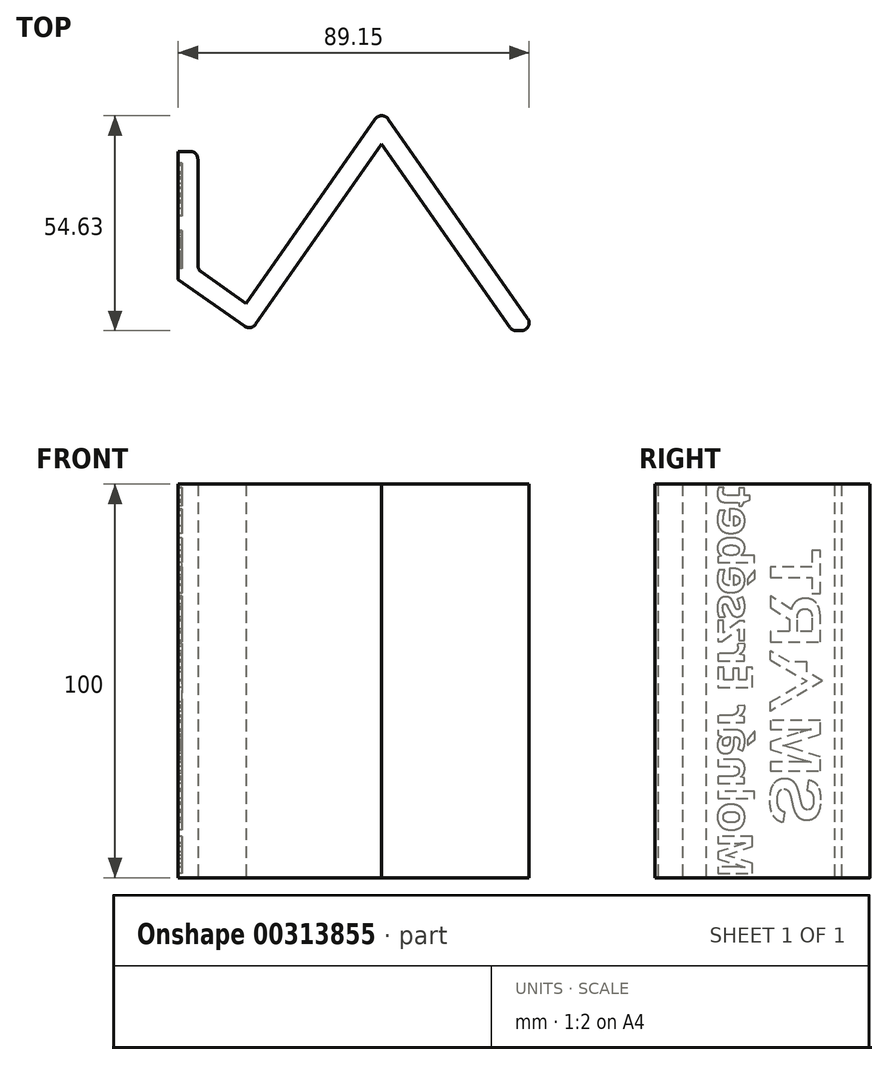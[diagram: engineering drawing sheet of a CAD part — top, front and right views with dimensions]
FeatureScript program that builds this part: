
annotation { "Feature Type Name" : "Feature", "Feature Type Description" : "" }
export const myFeature = defineFeature(function(context is Context, id is Id, definition is map)
    precondition{}
    {
        {
            var Q0;
            Q0=qCreatedBy(makeId("Top.planeOp"),FACE);
            var sketch = newSketch(context, id + "F0", { "sketchPlane" : qUnion([Q0])});
            skLineSegment(sketch, "E0", {"start": v(-30.75, -21.67) * mm, "end": v(-18.46, -30.27) * mm});
            skLineSegment(sketch, "E1", {"start": v(-18.46, -30.27) * mm, "end": v(15.96, 18.88) * mm});
            skLineSegment(sketch, "E2", {"start": v(15.96, 18.88) * mm, "end": v(37.02, -11.21) * mm});
            skLineSegment(sketch, "E3", {"start": v(-30.75, -21.67) * mm, "end": v(-30.75, 8.33) * mm});
            skLineSegment(sketch, "E4", {"start": v(-45.81, -37.24) * mm, "end": v(46.59, -37.24) * mm, "construction": true});
            skLineSegment(sketch, "E5.0", {"start": v(-35.75, -24.27) * mm, "end": v(-35.75, 8.33) * mm});
            skLineSegment(sketch, "E5.1", {"start": v(-35.75, -24.27) * mm, "end": v(-17.23, -37.24) * mm});
            skLineSegment(sketch, "E5.2", {"start": v(-17.23, -37.24) * mm, "end": v(15.96, 10.16) * mm});
            skLineSegment(sketch, "E5.3", {"start": v(15.96, 10.16) * mm, "end": v(49.14, -37.24) * mm});
            skLineSegment(sketch, "E6", {"start": v(-35.75, 8.33) * mm, "end": v(-30.75, 8.33) * mm});
            skLineSegment(sketch, "E7", {"start": v(49.14, -37.24) * mm, "end": v(55.25, -37.24) * mm});
            skLineSegment(sketch, "E8", {"start": v(37.02, -11.21) * mm, "end": v(55.25, -37.24) * mm});
            skSolve(sketch);
        }
        {
            var Q0;
            Q0=makeQuery(id+"F0.imprint","IMPRINT",FACE,{"disambiguationData":[TD([[makeQuery(id+"F0.imprint","IMPRINT",EDGE,{"derivedFrom":sQuery(id+"F0.wireOp",EDGE,"E0")}),-1.0]])]});
            extrude(context, id + "F1", {"entities" : qUnion([Q0]), "depth" : 100 * mm});
        }
        {
            var Q0;
            Q0=makeQuery(id+"F1.opExtrude","SWEPT_EDGE",EDGE,{"disambiguationData":[OSD([sQuery(id+"F0.wireOp",EDGE,"E5.1"),sQuery(id+"F0.wireOp",EDGE,"E5.2")])]});
            var Q1;
            Q1=makeQuery(id+"F1.opExtrude","SWEPT_EDGE",EDGE,{"disambiguationData":[OSD([sQuery(id+"F0.wireOp",EDGE,"E5.3"),sQuery(id+"F0.wireOp",EDGE,"E7")])]});
            var Q2;
            Q2=makeQuery(id+"F1.opExtrude","SWEPT_EDGE",EDGE,{"disambiguationData":[OSD([sQuery(id+"F0.wireOp",EDGE,"E7"),sQuery(id+"F0.wireOp",EDGE,"E8")])]});
            var Q3;
            Q3=makeQuery(id+"F1.opExtrude","SWEPT_EDGE",EDGE,{"disambiguationData":[OSD([sQuery(id+"F0.wireOp",EDGE,"E1"),sQuery(id+"F0.wireOp",EDGE,"E2")])]});
            var Q4;
            Q4=makeQuery(id+"F1.opExtrude","SWEPT_EDGE",EDGE,{"disambiguationData":[OSD([sQuery(id+"F0.wireOp",EDGE,"E0"),sQuery(id+"F0.wireOp",EDGE,"E3")])]});
            var Q5;
            Q5=makeQuery(id+"F1.opExtrude","SWEPT_EDGE",EDGE,{"disambiguationData":[OSD([sQuery(id+"F0.wireOp",EDGE,"E3"),sQuery(id+"F0.wireOp",EDGE,"E6")])]});
            fillet(context, id + "F2", {"entities" : qUnion([Q0, Q1, Q2, Q3, Q4, Q5]), "radius" : 2 * mm, "tangentPropagation" : true, "allowEdgeOverflow" : false});
        }
        {
            var Q0;
            Q0=makeQuery(id+"F1.opExtrude","SWEPT_FACE",FACE,{"disambiguationData":[OSD([sQuery(id+"F0.wireOp",EDGE,"E5.0")])]});
            var sketch = newSketch(context, id + "F3", { "sketchPlane" : qUnion([Q0])});
            skLineSegment(sketch, "E9", {"start": v(24.27, 50) * mm, "end": v(-8.33, 50) * mm, "construction": true});
            skLineSegment(sketch, "E10", {"start": v(7.97, 0) * mm, "end": v(7.97, 100) * mm, "construction": true});
            skText(sketch, "E11", { "text": "Molnár Erzsébet", "fontName": "OpenSans-Bold.ttf"});
            skLineSegment(sketch, "E12", {"start": v(21.27, 0) * mm, "end": v(21.27, 100) * mm, "construction": true});
            skLineSegment(sketch, "E13", {"start": v(-5.33, 0) * mm, "end": v(-5.33, 100) * mm, "construction": true});
            skLineSegment(sketch, "E14", {"start": v(-5.33, 50) * mm, "end": v(7.97, 42.32) * mm});
            skLineSegment(sketch, "E15", {"start": v(7.97, 42.32) * mm, "end": v(7.97, 44.63) * mm});
            skLineSegment(sketch, "E16", {"start": v(7.97, 44.63) * mm, "end": v(-1.33, 50) * mm});
            skLineSegment(sketch, "E17.MirrorCS", {"start": v(7.97, 55.37) * mm, "end": v(-1.33, 50) * mm});
            skLineSegment(sketch, "E18.MirrorCS", {"start": v(-5.33, 50) * mm, "end": v(-1.33, 52.3) * mm});
            skLineSegment(sketch, "E19", {"start": v(7.97, 55.37) * mm, "end": v(7.97, 57.68) * mm});
            skLineSegment(sketch, "E20", {"start": v(-1.33, 52.3) * mm, "end": v(-1.33, 54.89) * mm});
            skLineSegment(sketch, "E21", {"start": v(-1.33, 54.89) * mm, "end": v(3.14, 54.89) * mm});
            skLineSegment(sketch, "E22.trimOffspring", {"start": v(3.14, 54.89) * mm, "end": v(7.97, 57.68) * mm});
            skLineSegment(sketch, "E23", {"start": v(7.97, 41.32) * mm, "end": v(-5.33, 41.32) * mm, "construction": true});
            skLineSegment(sketch, "E24", {"start": v(7.97, 58.68) * mm, "end": v(-5.33, 58.68) * mm, "construction": true});
            skText(sketch, "E25", { "text": "SM", "fontName": "Arimo-Bold.ttf"});
            skText(sketch, "E26", { "text": "RT", "fontName": "Arimo-Bold.ttf"});
            skLineSegment(sketch, "E27", {"start": v(-5.33, 98) * mm, "end": v(21.27, 98) * mm, "construction": true});
            skLineSegment(sketch, "E28", {"start": v(-5.33, 2) * mm, "end": v(21.27, 2) * mm, "construction": true});
            const initialGuessF3  = {"E11": [0.02127, 0, 0, 1, 0.00886], "E25": [0.00797, 0.01356, 0, 1, 0.0133], "E26": [0.00797, 0.05868, 0, 1, 0.0133]};
            skSetInitialGuess(sketch, initialGuessF3);
            skSolve(sketch);
        }
        {
            var Q0;
            Q0=makeQuery(id+"F3.imprint","IMPRINT",FACE,{"disambiguationData":[TD([[makeQuery(id+"F3.imprint","IMPRINT",EDGE,{"derivedFrom":sQuery(id+"F3.wireOp",EDGE,"E11.sketch_text.stroke-37")}),-1.0]])]});
            var Q1;
            Q1=makeQuery(id+"F3.imprint","IMPRINT",FACE,{"disambiguationData":[TD([[makeQuery(id+"F3.imprint","IMPRINT",EDGE,{"derivedFrom":sQuery(id+"F3.wireOp",EDGE,"E11.sketch_text.stroke-0")}),-1.0]])]});
            var Q2;
            Q2=makeQuery(id+"F3.imprint","IMPRINT",FACE,{"disambiguationData":[TD([[makeQuery(id+"F3.imprint","IMPRINT",EDGE,{"derivedFrom":sQuery(id+"F3.wireOp",EDGE,"E11.sketch_text.stroke-19")}),-1.0]])]});
            var Q3;
            Q3=makeQuery(id+"F3.imprint","IMPRINT",FACE,{"disambiguationData":[TD([[makeQuery(id+"F3.imprint","IMPRINT",EDGE,{"derivedFrom":sQuery(id+"F3.wireOp",EDGE,"E11.sketch_text.stroke-41")}),-1.0]])]});
            var Q4;
            Q4=makeQuery(id+"F3.imprint","IMPRINT",FACE,{"disambiguationData":[TD([[makeQuery(id+"F3.imprint","IMPRINT",EDGE,{"derivedFrom":sQuery(id+"F3.wireOp",EDGE,"E11.sketch_text.stroke-58")}),-1.0]])]});
            var Q5;
            Q5=makeQuery(id+"F3.imprint","IMPRINT",FACE,{"disambiguationData":[TD([[makeQuery(id+"F3.imprint","IMPRINT",EDGE,{"derivedFrom":sQuery(id+"F3.wireOp",EDGE,"E11.sketch_text.stroke-90")}),-1.0]])]});
            var Q6;
            Q6=makeQuery(id+"F3.imprint","IMPRINT",FACE,{"disambiguationData":[TD([[makeQuery(id+"F3.imprint","IMPRINT",EDGE,{"derivedFrom":sQuery(id+"F3.wireOp",EDGE,"E11.sketch_text.stroke-83")}),-1.0]])]});
            var Q7;
            Q7=makeQuery(id+"F3.imprint","IMPRINT",FACE,{"disambiguationData":[TD([[makeQuery(id+"F3.imprint","IMPRINT",EDGE,{"derivedFrom":sQuery(id+"F3.wireOp",EDGE,"E11.sketch_text.stroke-103")}),-1.0]])]});
            var Q8;
            Q8=makeQuery(id+"F3.imprint","IMPRINT",FACE,{"disambiguationData":[TD([[makeQuery(id+"F3.imprint","IMPRINT",EDGE,{"derivedFrom":sQuery(id+"F3.wireOp",EDGE,"E11.sketch_text.stroke-115")}),-1.0]])]});
            var Q9;
            Q9=makeQuery(id+"F3.imprint","IMPRINT",FACE,{"disambiguationData":[TD([[makeQuery(id+"F3.imprint","IMPRINT",EDGE,{"derivedFrom":sQuery(id+"F3.wireOp",EDGE,"E11.sketch_text.stroke-128")}),-1.0]])]});
            var Q10;
            Q10=makeQuery(id+"F3.imprint","IMPRINT",FACE,{"disambiguationData":[TD([[makeQuery(id+"F3.imprint","IMPRINT",EDGE,{"derivedFrom":sQuery(id+"F3.wireOp",EDGE,"E11.sketch_text.stroke-138")}),-1.0]])]});
            var Q11;
            Q11=makeQuery(id+"F3.imprint","IMPRINT",FACE,{"disambiguationData":[TD([[makeQuery(id+"F3.imprint","IMPRINT",EDGE,{"derivedFrom":sQuery(id+"F3.wireOp",EDGE,"E11.sketch_text.stroke-164")}),-1.0]])]});
            var Q12;
            Q12=makeQuery(id+"F3.imprint","IMPRINT",FACE,{"disambiguationData":[TD([[makeQuery(id+"F3.imprint","IMPRINT",EDGE,{"derivedFrom":sQuery(id+"F3.wireOp",EDGE,"E11.sketch_text.stroke-184")}),-1.0]])]});
            var Q13;
            Q13=makeQuery(id+"F3.imprint","IMPRINT",FACE,{"disambiguationData":[TD([[makeQuery(id+"F3.imprint","IMPRINT",EDGE,{"derivedFrom":sQuery(id+"F3.wireOp",EDGE,"E11.sketch_text.stroke-191")}),-1.0]])]});
            var Q14;
            Q14=makeQuery(id+"F3.imprint","IMPRINT",FACE,{"disambiguationData":[TD([[makeQuery(id+"F3.imprint","IMPRINT",EDGE,{"derivedFrom":sQuery(id+"F3.wireOp",EDGE,"E11.sketch_text.stroke-214")}),-1.0]])]});
            var Q15;
            Q15=makeQuery(id+"F3.imprint","IMPRINT",FACE,{"disambiguationData":[TD([[makeQuery(id+"F3.imprint","IMPRINT",EDGE,{"derivedFrom":sQuery(id+"F3.wireOp",EDGE,"E11.sketch_text.stroke-234")}),-1.0]])]});
            var Q16;
            Q16=makeQuery(id+"F3.imprint","IMPRINT",FACE,{"disambiguationData":[TD([[makeQuery(id+"F3.imprint","IMPRINT",EDGE,{"derivedFrom":sQuery(id+"F3.wireOp",EDGE,"E25.sketch_text.stroke-0")}),-1.0]])]});
            var Q17;
            Q17=makeQuery(id+"F3.imprint","IMPRINT",FACE,{"disambiguationData":[TD([[makeQuery(id+"F3.imprint","IMPRINT",EDGE,{"derivedFrom":sQuery(id+"F3.wireOp",EDGE,"E25.sketch_text.stroke-31")}),-1.0]])]});
            var Q18;
            Q18=makeQuery(id+"F3.imprint","IMPRINT",FACE,{"disambiguationData":[TD([[makeQuery(id+"F3.imprint","IMPRINT",EDGE,{"derivedFrom":sQuery(id+"F3.wireOp",EDGE,"E14")}),1.0]])]});
            var Q19;
            Q19=makeQuery(id+"F3.imprint","IMPRINT",FACE,{"disambiguationData":[TD([[makeQuery(id+"F3.imprint","IMPRINT",EDGE,{"derivedFrom":sQuery(id+"F3.wireOp",EDGE,"E26.sketch_text.stroke-0")}),-1.0]])]});
            var Q20;
            Q20=makeQuery(id+"F3.imprint","IMPRINT",FACE,{"disambiguationData":[TD([[makeQuery(id+"F3.imprint","IMPRINT",EDGE,{"derivedFrom":sQuery(id+"F3.wireOp",EDGE,"E26.sketch_text.stroke-18")}),-1.0]])]});
            extrude(context, id + "F4", {"entities" : qUnion([Q0, Q1, Q2, Q3, Q4, Q5, Q6, Q7, Q8, Q9, Q10, Q11, Q12, Q13, Q14, Q15, Q16, Q17, Q18, Q19, Q20]), "operationType" : NewBodyOperationType.REMOVE, "oppositeDirection" : true, "depth" : 1 * mm});
        }
    });
